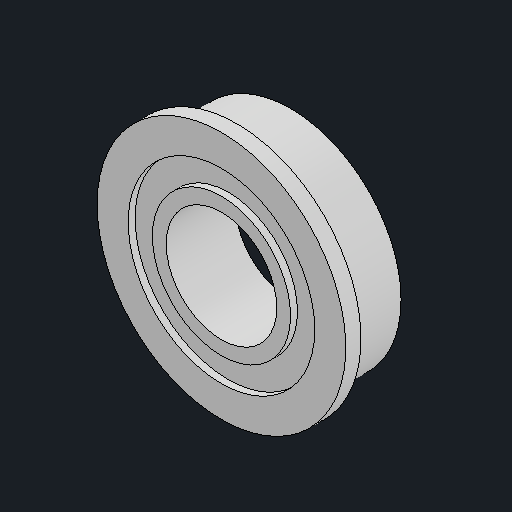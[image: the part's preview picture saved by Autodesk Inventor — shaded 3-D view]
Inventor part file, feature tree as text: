
AUTODESK INVENTOR PART (.ipt)
format: ipt  version: 2024.2 (Build 282272000, 272)  size: 109,568 bytes
history: native  units: mm
features: other x1, mirror x1
ambient origin geometry x8: Origin, YZ Plane, XZ Plane, XY Plane, X Axis, Y Axis, Z Axis, Center Point
bodies: Body1 (feature_tree)
feature tree (2):
  other  "솔리드1"
  mirror  "Mirror1"
